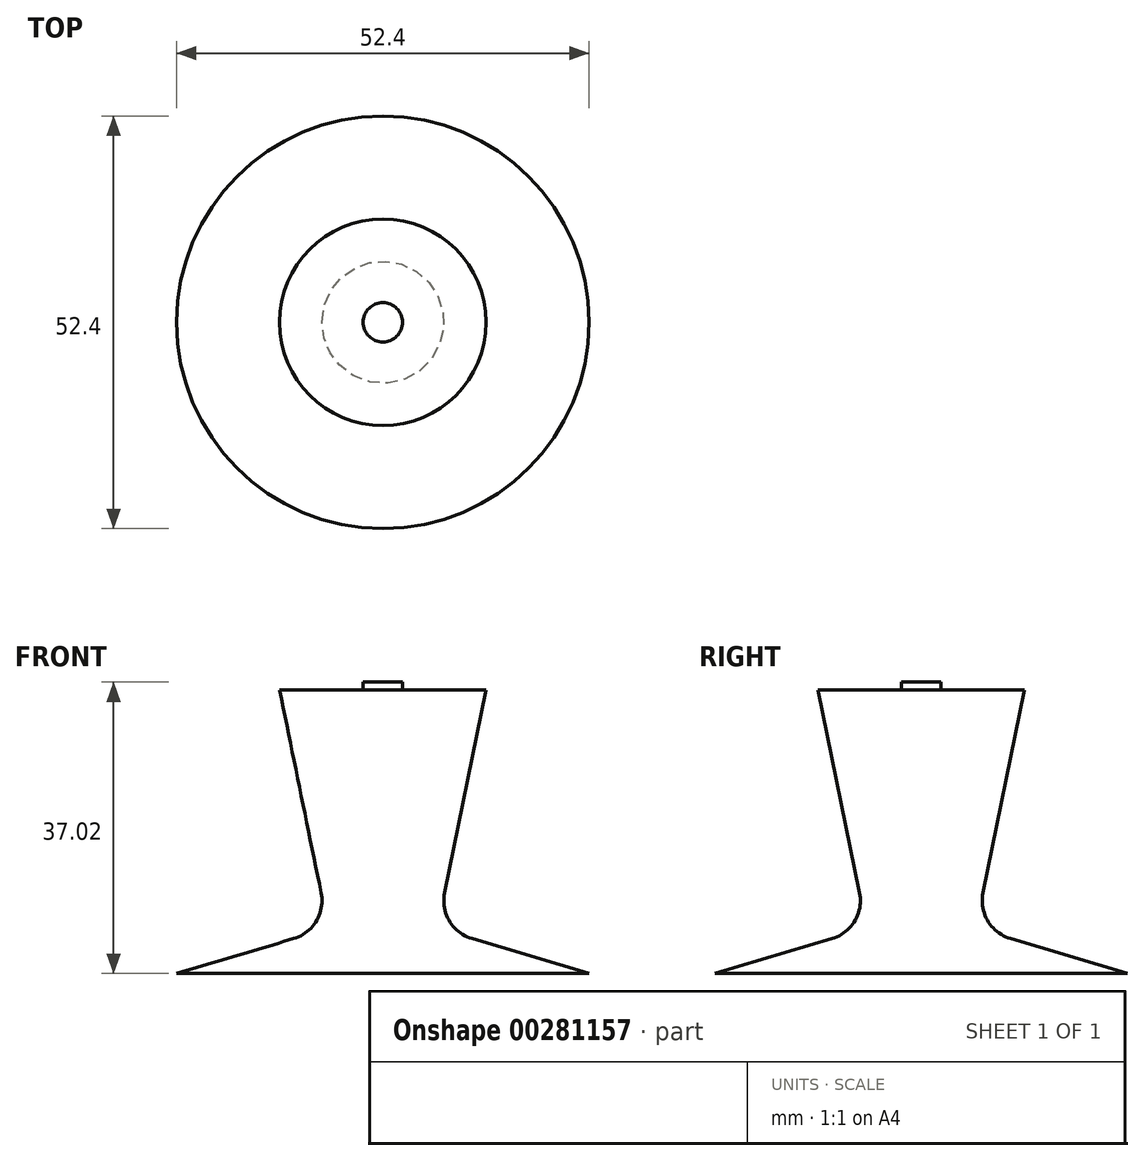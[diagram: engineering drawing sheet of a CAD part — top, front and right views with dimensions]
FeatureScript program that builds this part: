
annotation { "Feature Type Name" : "Feature", "Feature Type Description" : "" }
export const myFeature = defineFeature(function(context is Context, id is Id, definition is map)
    precondition{}
    {
        {
            var Q0;
            Q0=qCreatedBy(makeId("Right.planeOp"),FACE);
            var sketch = newSketch(context, id + "F0", { "sketchPlane" : qUnion([Q0])});
            skLineSegment(sketch, "E0", {"start": v(-13.12, 2.92) * mm, "end": v(-7.84, -22.88) * mm});
            skLineSegment(sketch, "E1", {"start": v(-11.32, -28.67) * mm, "end": v(-26.2, -33.1) * mm});
            skLineSegment(sketch, "E2", {"start": v(-26.2, -33.1) * mm, "end": v(0, -33.1) * mm});
            skLineSegment(sketch, "E3", {"start": v(0, -33.1) * mm, "end": v(0, 2.92) * mm});
            skLineSegment(sketch, "E4", {"start": v(-13.12, 2.92) * mm, "end": v(0, 2.92) * mm});
            skPoint(sketch, "E5.visualSharp", {"position": v(-6.93, -27.36) * mm});
            skArc(sketch, "E5.filletArc", {"start": v(-11.32, -28.67) * mm, "mid": v(-8.45, -26.45) * mm, "end": v(-7.84, -22.88) * mm});
            skSolve(sketch);
        }
        {
            var Q0;
            Q0=makeQuery(id+"F0.imprint","IMPRINT",FACE,{"disambiguationData":[TD([[makeQuery(id+"F0.imprint","IMPRINT",EDGE,{"derivedFrom":sQuery(id+"F0.wireOp",EDGE,"E0")}),1.0]])]});
            var Q1;
            Q1=sQuery(id+"F0.wireOp",EDGE,"E3");
            revolve(context, id + "F1", {"entities" : qUnion([Q0]), "axis" : qUnion([Q1]), "revolveType" : RevolveType.FULL});
        }
        {
            var Q0;
            Q0=makeQuery(id+"F1.opRevolve","SWEPT_FACE",FACE,{"disambiguationData":[OSD([sQuery(id+"F0.wireOp",EDGE,"E4")])]});
            var sketch = newSketch(context, id + "F2", { "sketchPlane" : qUnion([Q0])});
            skCircle(sketch, "E6", {"center": v(0, 0) * mm, "radius": 2.5 * mm});
            skSolve(sketch);
        }
        {
            var Q0;
            Q0=makeQuery(id+"F2.imprint","IMPRINT",FACE,{"disambiguationData":[TD([[makeQuery(id+"F2.imprint","IMPRINT",EDGE,{"derivedFrom":sQuery(id+"F2.wireOp",EDGE,"E6")}),1.0]])]});
            extrude(context, id + "F3", {"entities" : qUnion([Q0]), "operationType" : NewBodyOperationType.ADD, "depth" : 1 * mm});
        }
    });
